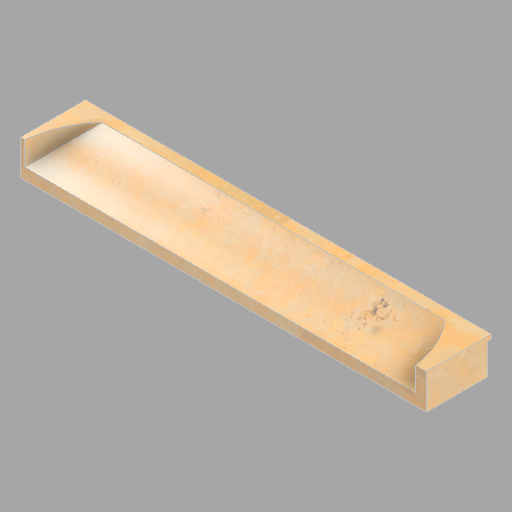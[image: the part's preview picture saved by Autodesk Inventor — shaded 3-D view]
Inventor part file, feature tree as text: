
AUTODESK INVENTOR PART (.ipt)
format: ipt  version: 2022.2 (Build 262287010, 287A)  size: 227,328 bytes
history: native  units: in
note: dims shown in document units (in); Inventor stores cm internally (conversion verified against a paired STEP export)
features: other x1, direct_edit x1, revolve x1
ambient origin geometry x8: Origin, YZ Plane, XZ Plane, XY Plane, X Axis, Y Axis, Z Axis, Center Point
bodies: Solid1 (feature_tree)
feature tree (3):
  other  "North (4) (1)"
  direct_edit  "Direct Edit1"
  revolve  "Rotate1"  Angle=90.0deg
